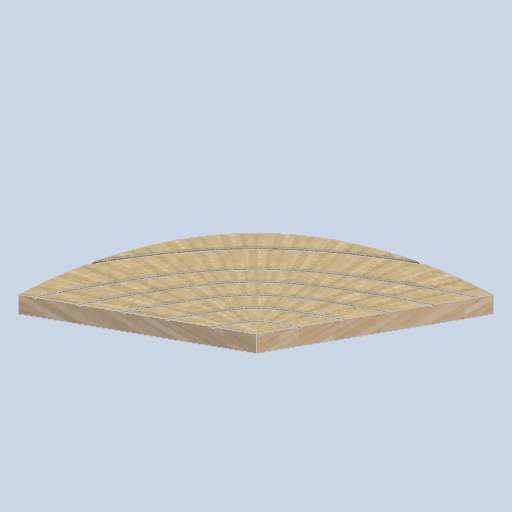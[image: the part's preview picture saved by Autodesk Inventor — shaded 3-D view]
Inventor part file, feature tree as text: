
AUTODESK INVENTOR PART (.ipt)
format: ipt  version: 2024.2 (Build 282272000, 272)  size: 857,088 bytes
history: native  units: in
note: dims shown in document units (in); Inventor stores cm internally (conversion verified against a paired STEP export)
features: sketch x19, plane x6, other x3
ambient origin geometry x8: Origin, YZ Plane, XZ Plane, XY Plane, X Axis, Y Axis, Z Axis, Center Point
bodies: Solid1 (feature_tree)
feature tree (28):
  other  "side_curve_corner_panel.ipt"
  other  "Solid1::side_curve_corner_panel.ipt"
  other  "TaggingFeature1"
  sketch  "Sketch1"  dims[d0=0.3937in]
  sketch  "Sketch2"
  sketch  "Sketch3"
  sketch  "Sketch4"
  sketch  "Sketch5"
  sketch  "Sketch6"
  sketch  "Sketch7"
  sketch  "Sketch8"
  sketch  "Sketch9"
  sketch  "Sketch10"
  sketch  "Sketch11"
  sketch  "Sketch12"
  sketch  "Sketch13"
  sketch  "Sketch14"
  sketch  "Sketch15"
  sketch  "Sketch16"
  sketch  "Sketch17"
  sketch  "Sketch18"
  sketch  "Sketch19"
  plane  "Work Plane1"
  plane  "Work Plane2"
  plane  "Work Plane3"
  plane  "Work Plane4"
  plane  "Work Plane5"
  plane  "Work Plane6"
